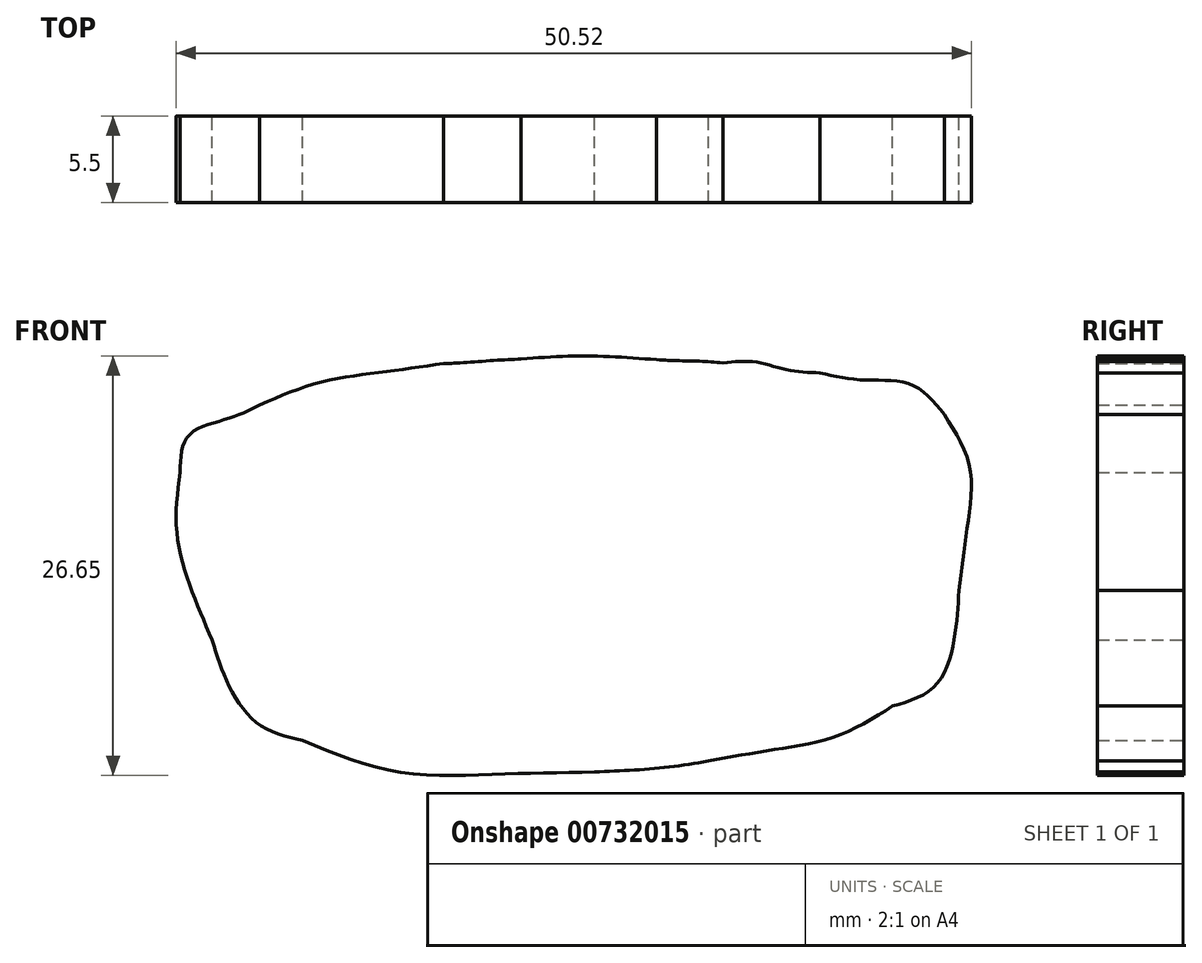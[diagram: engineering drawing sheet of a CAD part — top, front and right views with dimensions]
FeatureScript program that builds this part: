
annotation { "Feature Type Name" : "Feature", "Feature Type Description" : "" }
export const myFeature = defineFeature(function(context is Context, id is Id, definition is map)
    precondition{}
    {
        {
            var Q0;
            Q0=qCreatedBy(makeId("Front.planeOp"),FACE);
            var sketch = newSketch(context, id + "F0", { "sketchPlane" : qUnion([Q0])});
            skFitSpline(sketch, "E0", {"points": [v(0.68, -12.25) * mm, v(-5.55, -12.4) * mm, v(-11.93, -12.23) * mm, v(-17.9, -10.24) * mm]});
            skFitSpline(sketch, "E1", {"points": [v(-17.9, -10.24) * mm, v(-20.71, -9.18) * mm, v(-22.62, -6.63) * mm, v(-23.62, -3.87) * mm]});
            skFitSpline(sketch, "E2", {"points": [v(-23.62, -3.87) * mm, v(-24.99, -0.52) * mm, v(-25.88, 3.13) * mm, v(-25.66, 6.76) * mm]});
            skFitSpline(sketch, "E3", {"points": [v(-25.66, 6.76) * mm, v(-25.11, 9.13) * mm, v(-22.6, 10.2) * mm, v(-20.6, 11.07) * mm]});
            skFitSpline(sketch, "E4", {"points": [v(-20.6, 11.07) * mm, v(-16.85, 12.47) * mm, v(-12.88, 13.14) * mm, v(-8.93, 13.69) * mm]});
            skFitSpline(sketch, "E5", {"points": [v(-8.93, 13.69) * mm, v(-7.78, 13.74) * mm, v(-5.71, 13.89) * mm, v(-4, 13.98) * mm]});
            skFitSpline(sketch, "E6", {"points": [v(-4, 13.98) * mm, v(-1.13, 14.15) * mm, v(1.74, 14.13) * mm, v(4.6, 13.94) * mm]});
            skFitSpline(sketch, "E7", {"points": [v(4.6, 13.94) * mm, v(6, 13.87) * mm, v(7.36, 13.84) * mm, v(8.82, 13.73) * mm]});
            skFitSpline(sketch, "E8", {"points": [v(8.82, 13.73) * mm, v(10.88, 13.8) * mm, v(12.93, 13.28) * mm, v(14.99, 13.1) * mm]});
            skFitSpline(sketch, "E9", {"points": [v(14.99, 13.1) * mm, v(17.7, 12.65) * mm, v(20.74, 12.37) * mm, v(22.88, 10.45) * mm]});
            skFitSpline(sketch, "E10", {"points": [v(22.88, 10.45) * mm, v(24.5, 7) * mm, v(24.3, 2.98) * mm, v(23.8, -0.72) * mm]});
            skFitSpline(sketch, "E11", {"points": [v(23.8, -0.72) * mm, v(23.54, -3.61) * mm, v(22.36, -6.72) * mm, v(19.6, -8.07) * mm]});
            skFitSpline(sketch, "E12", {"points": [v(19.6, -8.07) * mm, v(15.99, -10) * mm, v(11.9, -10.86) * mm, v(7.9, -11.56) * mm]});
            skFitSpline(sketch, "E13", {"points": [v(7.9, -11.56) * mm, v(5.5, -11.92) * mm, v(3.1, -12.14) * mm, v(0.68, -12.25) * mm]});
            skSolve(sketch);
        }
        {
            var Q0;
            Q0 = qSketchRegion(id + "F0", true);
            extrude(context, id + "F1", {"entities" : qUnion([Q0]), "depth" : 5.5 * mm, "offsetDistance" : 25 * mm});
        }
    });
